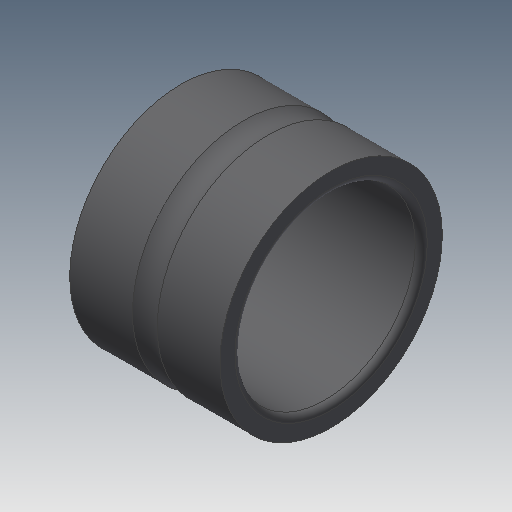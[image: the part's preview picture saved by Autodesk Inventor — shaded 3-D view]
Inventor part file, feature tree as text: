
AUTODESK INVENTOR PART (.ipt)
format: ipt  version: 2019.4 (Build 234330000, 330)  size: 201,728 bytes
history: native  units: mm
features: other x98, revolve x1, sketch x1
ambient origin geometry x8: Origin, YZ Plane, XZ Plane, XY Plane, X Axis, Y Axis, Z Axis, Center Point
bodies: Solid1 (feature_tree)
feature tree (100):
  revolve  "Revolution1"  [1 undecoded]
  other  "ip_st_1_1_XY"
  other  "ip_st_1_1_YZ"
  other  "ip_st_1_1_ZX"
  other  "ip_st_1_1_X"
  other  "ip_st_1_1_Y"
  other  "ip_st_1_1_Z"
  other  "ip_st_1_1_Center"
  other  "ip_st_1_10_XY"
  other  "ip_st_1_10_YZ"
  other  "ip_st_1_10_ZX"
  other  "ip_st_1_10_X"
  other  "ip_st_1_10_Y"
  other  "ip_st_1_10_Z"
  other  "ip_st_1_10_Center"
  other  "ip_st_1_11_XY"
  other  "ip_st_1_11_YZ"
  other  "ip_st_1_11_ZX"
  other  "ip_st_1_11_X"
  other  "ip_st_1_11_Y"
  other  "ip_st_1_11_Z"
  other  "ip_st_1_11_Center"
  other  "ip_st_1_12_XY"
  other  "ip_st_1_12_YZ"
  other  "ip_st_1_12_ZX"
  other  "ip_st_1_12_X"
  other  "ip_st_1_12_Y"
  other  "ip_st_1_12_Z"
  other  "ip_st_1_12_Center"
  other  "ip_st_1_2_XY"
  other  "ip_st_1_2_YZ"
  other  "ip_st_1_2_ZX"
  other  "ip_st_1_2_X"
  other  "ip_st_1_2_Y"
  other  "ip_st_1_2_Z"
  other  "ip_st_1_2_Center"
  other  "ip_st_1_3_XY"
  other  "ip_st_1_3_YZ"
  other  "ip_st_1_3_ZX"
  other  "ip_st_1_3_X"
  other  "ip_st_1_3_Y"
  other  "ip_st_1_3_Z"
  other  "ip_st_1_3_Center"
  other  "ip_st_1_4_XY"
  other  "ip_st_1_4_YZ"
  other  "ip_st_1_4_ZX"
  other  "ip_st_1_4_X"
  other  "ip_st_1_4_Y"
  other  "ip_st_1_4_Z"
  other  "ip_st_1_4_Center"
  other  "ip_st_1_5_XY"
  other  "ip_st_1_5_YZ"
  other  "ip_st_1_5_ZX"
  other  "ip_st_1_5_X"
  other  "ip_st_1_5_Y"
  other  "ip_st_1_5_Z"
  other  "ip_st_1_5_Center"
  other  "ip_st_1_6_XY"
  other  "ip_st_1_6_YZ"
  other  "ip_st_1_6_ZX"
  other  "ip_st_1_6_X"
  other  "ip_st_1_6_Y"
  other  "ip_st_1_6_Z"
  other  "ip_st_1_6_Center"
  other  "ip_st_1_7_XY"
  other  "ip_st_1_7_YZ"
  other  "ip_st_1_7_ZX"
  other  "ip_st_1_7_X"
  other  "ip_st_1_7_Y"
  other  "ip_st_1_7_Z"
  other  "ip_st_1_7_Center"
  other  "ip_st_1_8_XY"
  other  "ip_st_1_8_YZ"
  other  "ip_st_1_8_ZX"
  other  "ip_st_1_8_X"
  other  "ip_st_1_8_Y"
  other  "ip_st_1_8_Z"
  other  "ip_st_1_8_Center"
  other  "ip_st_1_9_XY"
  other  "ip_st_1_9_YZ"
  other  "ip_st_1_9_ZX"
  other  "ip_st_1_9_X"
  other  "ip_st_1_9_Y"
  other  "ip_st_1_9_Z"
  other  "ip_st_1_9_Center"
  other  "ip_st_1a_XY"
  other  "ip_st_1a_YZ"
  other  "ip_st_1a_ZX"
  other  "ip_st_1a_X"
  other  "ip_st_1a_Y"
  other  "ip_st_1a_Z"
  other  "ip_st_1a_Center"
  other  "ip_st_2a_XY"
  other  "ip_st_2a_YZ"
  other  "ip_st_2a_ZX"
  other  "ip_st_2a_X"
  other  "ip_st_2a_Y"
  other  "ip_st_2a_Z"
  other  "ip_st_2a_Center"
  sketch  "Sketch_1"  dims[d0=360.0deg d1=0.0mm]
note: 1 required parameter value undecoded (feature->parameter linkage not recoverable at this tier; creation-order binding heuristic only, values carry confidence <= 0.55)
